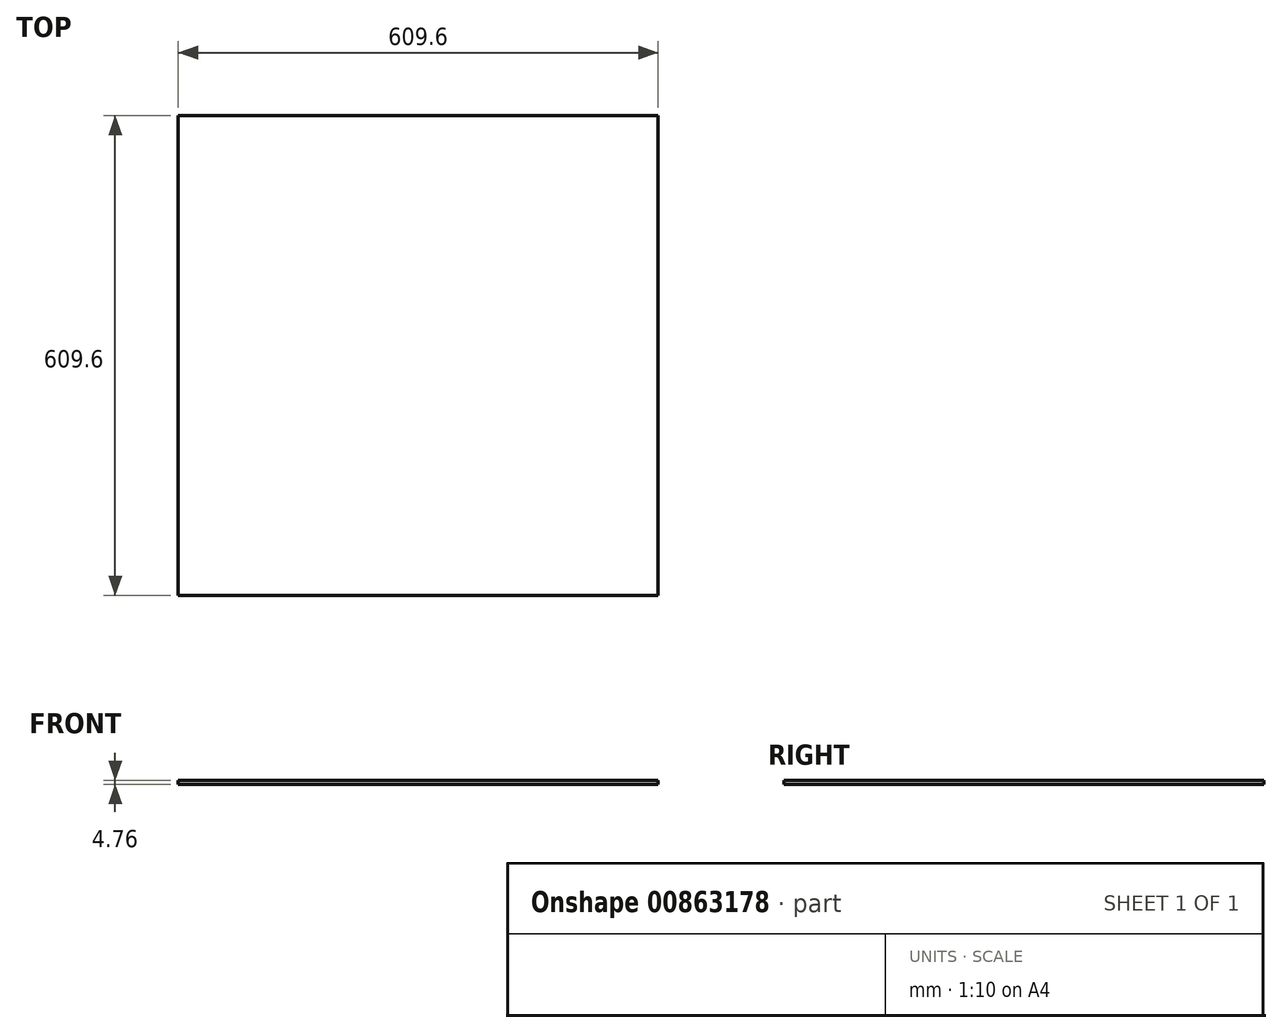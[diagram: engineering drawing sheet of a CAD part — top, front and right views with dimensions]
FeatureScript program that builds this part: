
annotation { "Feature Type Name" : "Feature", "Feature Type Description" : "" }
export const myFeature = defineFeature(function(context is Context, id is Id, definition is map)
    precondition{}
    {
        {
            var Q0;
            Q0=qCreatedBy(makeId("Top.planeOp"),FACE);
            var sketch = newSketch(context, id + "F0", { "sketchPlane" : qUnion([Q0])});
            skLineSegment(sketch, "E0.bottom", {"start": v(304.8, 304.8) * mm, "end": v(-304.8, 304.8) * mm});
            skLineSegment(sketch, "E0.top", {"start": v(304.8, -304.8) * mm, "end": v(-304.8, -304.8) * mm});
            skLineSegment(sketch, "E0.left", {"start": v(304.8, 304.8) * mm, "end": v(304.8, -304.8) * mm});
            skLineSegment(sketch, "E0.right", {"start": v(-304.8, 304.8) * mm, "end": v(-304.8, -304.8) * mm});
            skPoint(sketch, "E0.middle", {"position": v(0, 0) * mm});
            skSolve(sketch);
        }
        {
            var Q0;
            Q0=makeQuery(id+"F0.imprint","IMPRINT",FACE,{"disambiguationData":[TD([[makeQuery(id+"F0.imprint","IMPRINT",EDGE,{"derivedFrom":sQuery(id+"F0.wireOp",EDGE,"E0.bottom")}),1.0]])]});
            extrude(context, id + "F1", {"entities" : qUnion([Q0]), "depth" : 4.76 * mm, "offsetDistance" : 25.4 * mm});
        }
    });
